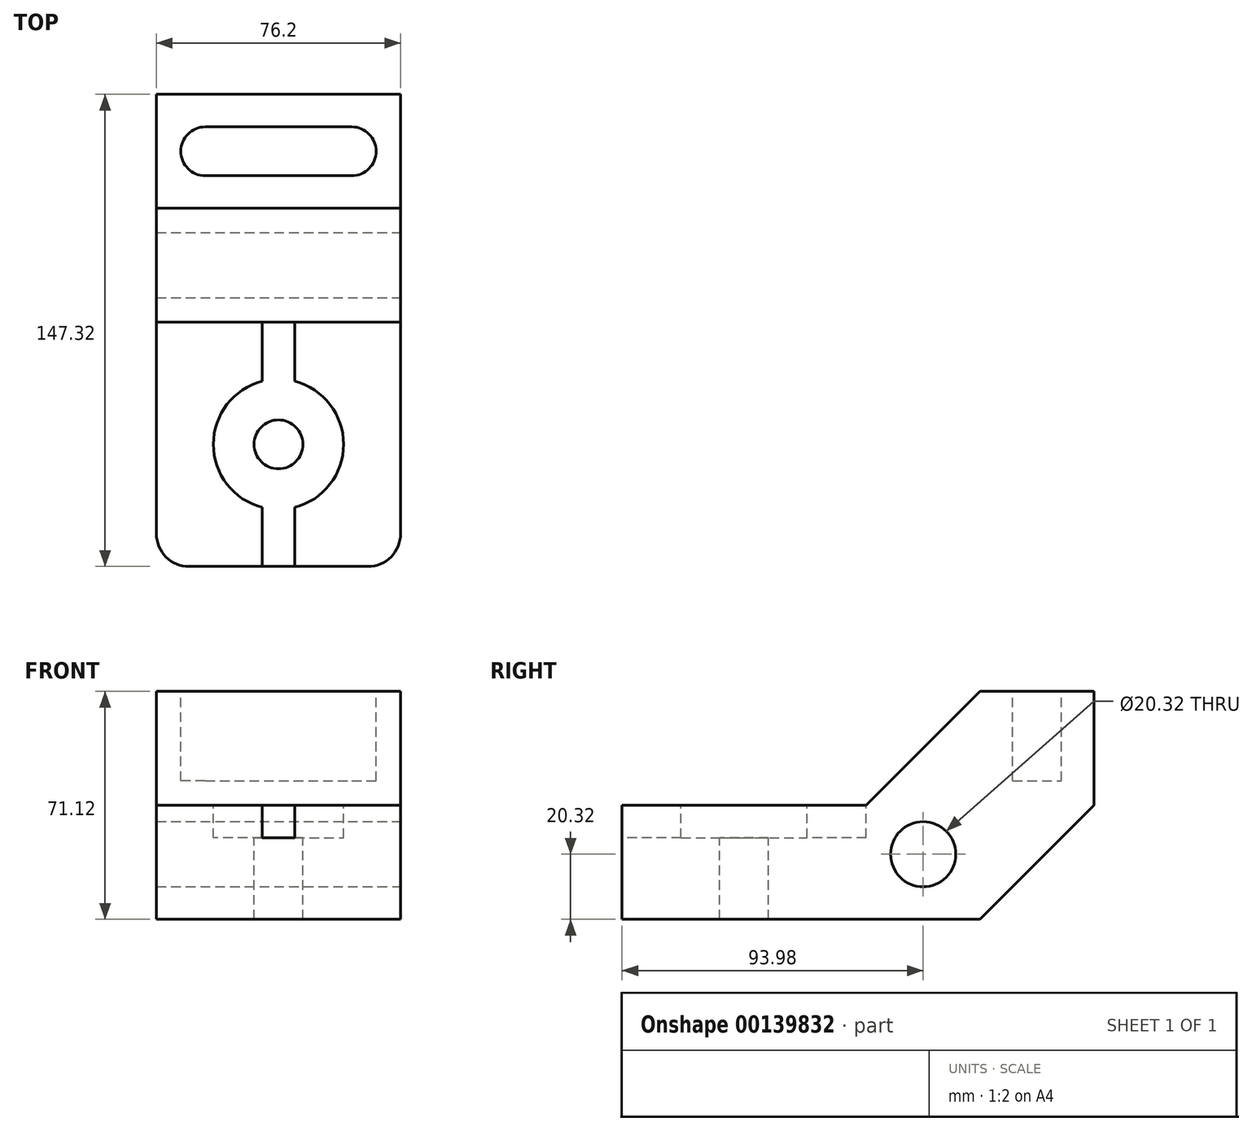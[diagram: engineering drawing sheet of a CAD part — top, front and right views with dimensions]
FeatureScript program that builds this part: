
annotation { "Feature Type Name" : "Feature", "Feature Type Description" : "" }
export const myFeature = defineFeature(function(context is Context, id is Id, definition is map)
    precondition{}
    {
        {
            var Q0;
            Q0=qCreatedBy(makeId("Right.planeOp"),FACE);
            var sketch = newSketch(context, id + "F0", { "sketchPlane" : qUnion([Q0])});
            skLineSegment(sketch, "E0", {"start": v(0, 0) * mm, "end": v(35.56, 35.56) * mm});
            skLineSegment(sketch, "E1", {"start": v(35.56, 35.56) * mm, "end": v(35.56, 71.12) * mm});
            skLineSegment(sketch, "E2", {"start": v(35.56, 71.12) * mm, "end": v(0, 71.12) * mm});
            skLineSegment(sketch, "E3", {"start": v(0, 71.12) * mm, "end": v(-35.56, 35.56) * mm});
            skLineSegment(sketch, "E4", {"start": v(-35.56, 35.56) * mm, "end": v(-111.76, 35.56) * mm});
            skLineSegment(sketch, "E5", {"start": v(-111.76, 35.56) * mm, "end": v(-111.76, 0) * mm});
            skLineSegment(sketch, "E6", {"start": v(-111.76, 0) * mm, "end": v(0, 0) * mm});
            skSolve(sketch);
        }
        {
            var Q0;
            Q0 = qSketchRegion(id + "F0", true);
            extrude(context, id + "F1", {"entities" : qUnion([Q0]), "endBound" : BoundingType.SYMMETRIC, "depth" : 76.2 * mm});
        }
        {
            var Q0;
            Q0=makeQuery(id+"F1.opExtrude","CAP_FACE",FACE,{"disambiguationData":[OSD([sQuery(id+"F0.wireOp",EDGE,"E0"),sQuery(id+"F0.wireOp",EDGE,"E1"),sQuery(id+"F0.wireOp",EDGE,"E2"),sQuery(id+"F0.wireOp",EDGE,"E3"),sQuery(id+"F0.wireOp",EDGE,"E4"),sQuery(id+"F0.wireOp",EDGE,"E5"),sQuery(id+"F0.wireOp",EDGE,"E6")])],"isStart":false});
            var sketch = newSketch(context, id + "F2", { "sketchPlane" : qUnion([Q0])});
            skCircle(sketch, "E7", {"center": v(-17.78, 20.32) * mm, "radius": 10.16 * mm});
            skSolve(sketch);
        }
        {
            var Q0;
            Q0 = qSketchRegion(id + "F2", true);
            extrude(context, id + "F3", {"entities" : qUnion([Q0]), "operationType" : NewBodyOperationType.REMOVE, "endBound" : BoundingType.THROUGH_ALL, "oppositeDirection" : true, "depth" : 25.4 * mm});
        }
        {
            var Q0;
            Q0=makeQuery(id+"F1.opExtrude","SWEPT_FACE",FACE,{"disambiguationData":[OSD([sQuery(id+"F0.wireOp",EDGE,"E2")])]});
            var sketch = newSketch(context, id + "F4", { "sketchPlane" : qUnion([Q0])});
            skLineSegment(sketch, "E8", {"start": v(-22.86, 25.4) * mm, "end": v(22.86, 25.4) * mm});
            skLineSegment(sketch, "E9", {"start": v(-22.86, 10.16) * mm, "end": v(22.86, 10.16) * mm});
            skArc(sketch, "E10", {"start": v(22.86, 25.4) * mm, "mid": v(30.48, 17.78) * mm, "end": v(22.86, 10.16) * mm});
            skArc(sketch, "E11", {"start": v(-22.86, 25.4) * mm, "mid": v(-30.48, 17.78) * mm, "end": v(-22.86, 10.16) * mm});
            skSolve(sketch);
        }
        {
            var Q0;
            Q0 = qSketchRegion(id + "F4", true);
            var Q1;
            Q1=makeQuery(id+"F4.imprint","IMPRINT",FACE,{"disambiguationData":[TD([[makeQuery(id+"F4.imprint","IMPRINT",EDGE,{"derivedFrom":sQuery(id+"F4.wireOp",EDGE,"E8")}),-1.0]])]});
            extrude(context, id + "F5", {"entities" : qUnion([Q0, Q1]), "operationType" : NewBodyOperationType.REMOVE, "oppositeDirection" : true, "depth" : 27.94 * mm});
        }
        {
            var Q0;
            Q0=makeQuery(id+"F1.opExtrude","SWEPT_FACE",FACE,{"disambiguationData":[OSD([sQuery(id+"F0.wireOp",EDGE,"E4")])]});
            var sketch = newSketch(context, id + "F6", { "sketchPlane" : qUnion([Q0])});
            skPoint(sketch, "E12", {"position": v(0, -73.66) * mm});
            skSolve(sketch);
        }
        {
            var Q0;
            Q0=sQuery(id+"F6.wireOp",VERTEX,"E12");
            var Q1;
            Q1=makeQuery(id+"F1.opExtrude","SWEPT_BODY",BODY,{"disambiguationData":[OSD([sQuery(id+"F0.wireOp",EDGE,"E0"),sQuery(id+"F0.wireOp",EDGE,"E1"),sQuery(id+"F0.wireOp",EDGE,"E2"),sQuery(id+"F0.wireOp",EDGE,"E3"),sQuery(id+"F0.wireOp",EDGE,"E4"),sQuery(id+"F0.wireOp",EDGE,"E5"),sQuery(id+"F0.wireOp",EDGE,"E6")])]});
            hole(context, id + "F7", {"style" : HoleStyle.C_BORE, "endStyle" : HoleEndStyle.THROUGH, "holeDiameter" : 15.24 * mm, "cBoreDiameter" : 40.64 * mm, "cBoreDepth" : 10.16 * mm, "locations" : qUnion([Q0]), "scope" : qUnion([Q1]), "isTappedThrough" : true});
        }
        {
            var Q0;
            Q0=makeQuery(id+"F1.opExtrude","SWEPT_FACE",FACE,{"disambiguationData":[OSD([sQuery(id+"F0.wireOp",EDGE,"E4")])]});
            var sketch = newSketch(context, id + "F8", { "sketchPlane" : qUnion([Q0])});
            skLineSegment(sketch, "E13", {"start": v(-5.08, -53.99) * mm, "end": v(-5.08, -35.56) * mm});
            skLineSegment(sketch, "E14", {"start": v(-5.08, -35.56) * mm, "end": v(5.08, -35.56) * mm});
            skLineSegment(sketch, "E15", {"start": v(5.08, -35.56) * mm, "end": v(5.08, -53.99) * mm});
            skLineSegment(sketch, "E16", {"start": v(-5.08, -93.33) * mm, "end": v(-5.08, -111.76) * mm});
            skLineSegment(sketch, "E17", {"start": v(-5.08, -111.76) * mm, "end": v(5.08, -111.76) * mm, "construction": true});
            skLineSegment(sketch, "E18", {"start": v(5.08, -111.76) * mm, "end": v(5.08, -93.33) * mm});
            skLineSegment(sketch, "E19", {"start": v(0, -24.81) * mm, "end": v(0, -120.88) * mm, "construction": true});
            skPoint(sketch, "E19.startSnap0", {"position": v(0, -35.56) * mm});
            skPoint(sketch, "E19.endSnap0", {"position": v(0, -111.76) * mm});
            skSolve(sketch);
        }
        {
            var Q0;
            Q0=makeQuery(id+"F1.opExtrude","CAP_EDGE",EDGE,{"disambiguationData":[OSD([sQuery(id+"F0.wireOp",EDGE,"E5")])],"isStart":false});
            var Q1;
            Q1=makeQuery(id+"F1.opExtrude","CAP_EDGE",EDGE,{"disambiguationData":[OSD([sQuery(id+"F0.wireOp",EDGE,"E5")])],"isStart":true});
            fillet(context, id + "F9", {"entities" : qUnion([Q0, Q1]), "radius" : 10.16 * mm, "tangentPropagation" : true, "allowEdgeOverflow" : false});
        }
        {
            var Q0;
            {var subQ0=sQuery(id+"F8.wireOp",EDGE,"E16");Q0=makeQuery(id+"F8.imprint","IMPRINT",FACE,{"disambiguationData":[TD([[makeQuery(id+"F8.imprint","IMPRINT",EDGE,{"derivedFrom":subQ0}),1.0]])]});}
            var Q1;
            {var subQ0=sQuery(id+"F8.wireOp",EDGE,"E13");Q1=makeQuery(id+"F8.imprint","IMPRINT",FACE,{"disambiguationData":[TD([[makeQuery(id+"F8.imprint","IMPRINT",EDGE,{"derivedFrom":subQ0}),-1.0]])]});}
            extrude(context, id + "F10", {"entities" : qUnion([Q0, Q1]), "operationType" : NewBodyOperationType.REMOVE, "oppositeDirection" : true, "depth" : 10.16 * mm});
        }
    });
